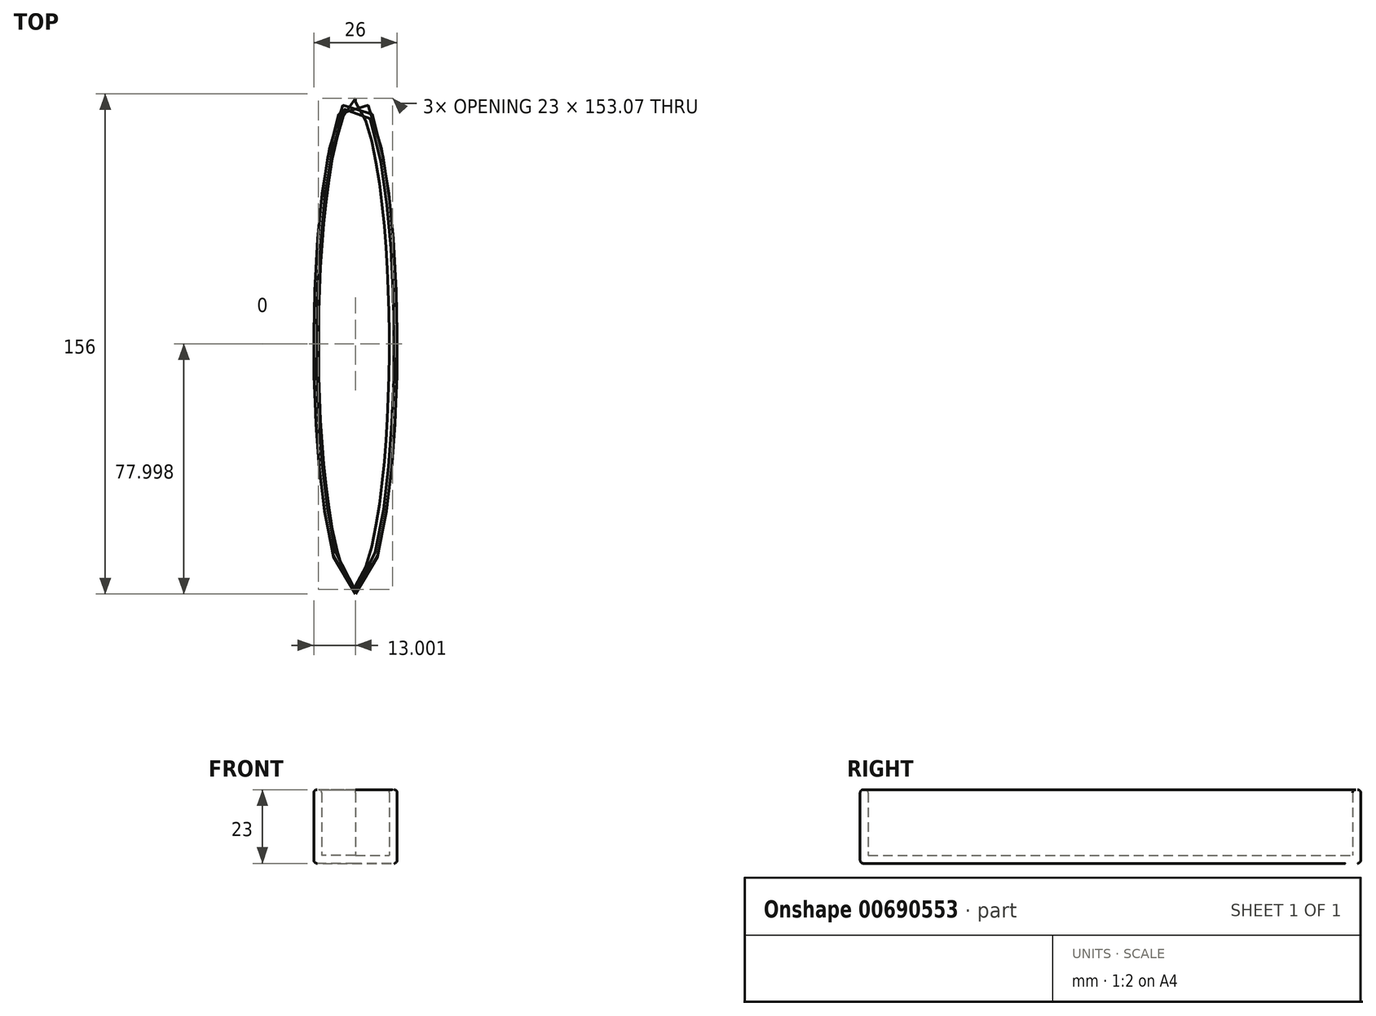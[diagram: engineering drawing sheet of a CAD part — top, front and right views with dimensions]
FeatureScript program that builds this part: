
annotation { "Feature Type Name" : "Feature", "Feature Type Description" : "" }
export const myFeature = defineFeature(function(context is Context, id is Id, definition is map)
    precondition{}
    {
        {
            var Q0;
            Q0=qCreatedBy(makeId("Top.planeOp"),FACE);
            var sketch = newSketch(context, id + "F0", { "sketchPlane" : qUnion([Q0])});
            skEllipse(sketch, "E0", {"center": v(-9.4, 29.6) * mm, "majorRadius": 75 * mm, "minorRadius": 10 * mm, "majorAxis": v(0, -1)});
            skSolve(sketch);
        }
        {
            var Q0;
            Q0=makeQuery(id+"F0.imprint","IMPRINT",FACE,{"disambiguationData":[TD([[makeQuery(id+"F0.imprint","IMPRINT",EDGE,{"derivedFrom":sQuery(id+"F0.wireOp",EDGE,"E0")}),1.0]])]});
            extrude(context, id + "F1", {"entities" : qUnion([Q0]), "depth" : 23 * mm, "offsetDistance" : 25 * mm});
        }
        {
            var Q0;
            Q0=qCreatedBy(makeId("Top.planeOp"),FACE);
            var sketch = newSketch(context, id + "F2", { "sketchPlane" : qUnion([Q0])});
            skEllipse(sketch, "E1", {"center": v(30.68, 31.99) * mm, "majorRadius": 78 * mm, "minorRadius": 13 * mm, "majorAxis": v(0, -1)});
            skSolve(sketch);
        }
        {
            var Q0;
            Q0=makeQuery(id+"F2.imprint","IMPRINT",FACE,{"disambiguationData":[TD([[makeQuery(id+"F2.imprint","IMPRINT",EDGE,{"derivedFrom":sQuery(id+"F2.wireOp",EDGE,"E1")}),1.0]])]});
            extrude(context, id + "F3", {"entities" : qUnion([Q0]), "depth" : 23 * mm, "offsetDistance" : 25 * mm});
        }
        {
            var Q0;
            Q0=makeQuery(id+"F1.opExtrude","CAP_FACE",FACE,{"disambiguationData":[OSD([sQuery(id+"F0.wireOp",EDGE,"E0")])],"isStart":false});
            var Q1;
            Q1=makeQuery(id+"F3.opExtrude","CAP_FACE",FACE,{"disambiguationData":[OSD([sQuery(id+"F2.wireOp",EDGE,"E1")])],"isStart":false});
            shell(context, id + "F4", {"entities" : qUnion([Q0, Q1]), "thickness" : 2.5 * mm});
        }
        {
            var Q0;
            {var subQ0=sQuery(id+"F0.wireOp",EDGE,"E0");Q0=makeQuery(id+"F4.opShell","OFFSET_EDGE",EDGE,{"disambiguationData":[OSD([subQ0]),TDD([makeQuery(id+"F1.opExtrude","CAP_EDGE",EDGE,{"disambiguationData":[OSD([subQ0])],"isStart":false})]),OD(1.0)]});}
            var Q1;
            Q1=makeQuery(id+"F1.opExtrude","CAP_EDGE",EDGE,{"disambiguationData":[OSD([sQuery(id+"F0.wireOp",EDGE,"E0")])],"isStart":false});
            var Q2;
            {var subQ0=sQuery(id+"F0.wireOp",EDGE,"E0");Q2=makeQuery(id+"F4.opShell","OFFSET_EDGE",EDGE,{"disambiguationData":[OSD([subQ0]),TDD([makeQuery(id+"F1.opExtrude","CAP_EDGE",EDGE,{"disambiguationData":[OSD([subQ0])],"isStart":false})]),OD(0.0)]});}
            var Q3;
            Q3=makeQuery(id+"F1.opExtrude","CAP_EDGE",EDGE,{"disambiguationData":[OSD([sQuery(id+"F0.wireOp",EDGE,"E0")])],"isStart":true});
            var Q4;
            Q4=makeQuery(id+"F3.opExtrude","CAP_EDGE",EDGE,{"disambiguationData":[OSD([sQuery(id+"F2.wireOp",EDGE,"E1")])],"isStart":true});
            var Q5;
            Q5=makeQuery(id+"F3.opExtrude","CAP_EDGE",EDGE,{"disambiguationData":[OSD([sQuery(id+"F2.wireOp",EDGE,"E1")])],"isStart":false});
            var Q6;
            {var subQ0=sQuery(id+"F2.wireOp",EDGE,"E1");Q6=makeQuery(id+"F4.opShell","OFFSET_EDGE",EDGE,{"disambiguationData":[OSD([subQ0]),TDD([makeQuery(id+"F3.opExtrude","CAP_EDGE",EDGE,{"disambiguationData":[OSD([subQ0])],"isStart":false})]),OD(0.0)]});}
            var Q7;
            {var subQ0=sQuery(id+"F2.wireOp",EDGE,"E1");Q7=makeQuery(id+"F4.opShell","OFFSET_EDGE",EDGE,{"disambiguationData":[OSD([subQ0]),TDD([makeQuery(id+"F3.opExtrude","CAP_EDGE",EDGE,{"disambiguationData":[OSD([subQ0])],"isStart":false})]),OD(1.0)]});}
            var Q8;
            {var subQ0=sQuery(id+"F0.wireOp",EDGE,"E0");Q8=makeQuery(id+"F4.opShell","OFFSET_EDGE",EDGE,{"disambiguationData":[OSD([subQ0]),TDD([makeQuery(id+"F1.opExtrude","CAP_EDGE",EDGE,{"disambiguationData":[OSD([subQ0])],"isStart":true})]),OD(1.0)]});}
            var Q9;
            {var subQ0=sQuery(id+"F0.wireOp",EDGE,"E0");Q9=makeQuery(id+"F4.opShell","OFFSET_EDGE",EDGE,{"disambiguationData":[OSD([subQ0]),TDD([makeQuery(id+"F1.opExtrude","CAP_EDGE",EDGE,{"disambiguationData":[OSD([subQ0])],"isStart":true})]),OD(0.0)]});}
            fillet(context, id + "F5", {"entities" : qUnion([Q0, Q1, Q2, Q3, Q4, Q5, Q6, Q7, Q8, Q9]), "radius" : 1 * mm, "tangentPropagation" : true, "allowEdgeOverflow" : false});
        }
    });
